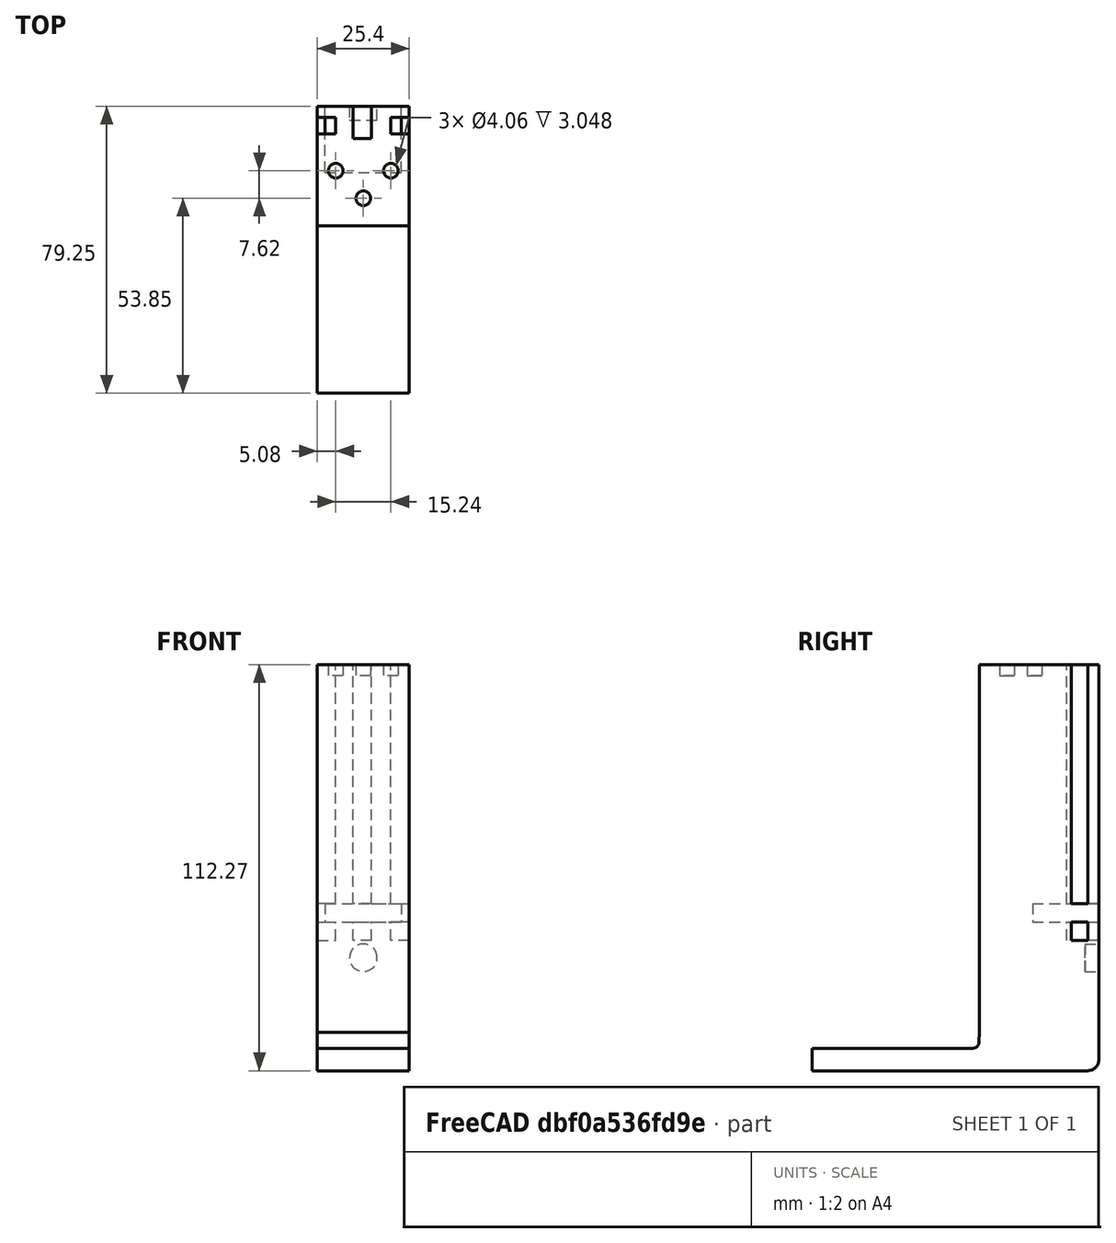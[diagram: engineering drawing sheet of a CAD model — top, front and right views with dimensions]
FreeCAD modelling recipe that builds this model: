
FCSTD DOCUMENT  (FreeCAD 0.18.1R)
Label: rail_test_crossbow_rev_02
License: All rights reserved
LicenseURL: http://en.wikipedia.org/wiki/All_rights_reserved
objects: Sketcher::SketchObject×7, PartDesign::Pad×4, PartDesign::Pocket×2, PartDesign::Hole×1, PartDesign::Body×1, Mesh::Feature×1
note: 22 computed .brp shape members not serialized (recipe doc carries the construction recipe); baked Part::Feature solids carry a one-line shape summary decoded from their .brp

FEATURE [Sketcher::SketchObject] Sketch
  MapMode = 5
  Support = -> [XY_Plane]
  sketch-geometry (17):
    g0: LineSegment StartX=0 StartY=0 StartZ=0 EndX=12.7 EndY=0 EndZ=0
    g1: LineSegment StartX=0 StartY=0 StartZ=0 EndX=-12.7 EndY=0 EndZ=0
    g2: LineSegment StartX=-12.7 StartY=0 StartZ=0 EndX=-12.7 EndY=25.4 EndZ=0
    g3: LineSegment StartX=12.7 StartY=0 StartZ=0 EndX=12.7 EndY=25.4 EndZ=0
    g4: LineSegment StartX=-12.7 StartY=25.4 StartZ=0 EndX=-7.62 EndY=25.4 EndZ=0
    g5: LineSegment StartX=-7.62 StartY=25.4 StartZ=0 EndX=-7.62 EndY=29.972 EndZ=0
    g6: LineSegment StartX=12.7 StartY=25.4 StartZ=0 EndX=7.62 EndY=25.4 EndZ=0
    g7: LineSegment StartX=7.62 StartY=25.4 StartZ=0 EndX=7.62 EndY=29.972 EndZ=0
    g8: LineSegment StartX=7.62 StartY=29.972 StartZ=0 EndX=12.7 EndY=29.972 EndZ=0
    g9: LineSegment StartX=-7.62 StartY=29.972 StartZ=0 EndX=-12.7 EndY=29.972 EndZ=0
    g10: LineSegment StartX=-12.7 StartY=29.972 StartZ=0 EndX=-12.7 EndY=33.02 EndZ=0
    g11: LineSegment StartX=12.7 StartY=29.972 StartZ=0 EndX=12.7 EndY=33.02 EndZ=0
    g12: LineSegment StartX=-12.7 StartY=33.02 StartZ=0 EndX=-2.794 EndY=33.02 EndZ=0
    g13: LineSegment StartX=-2.794 StartY=33.02 StartZ=0 EndX=-2.794 EndY=24.13 EndZ=0
    g14: LineSegment StartX=-2.794 StartY=24.13 StartZ=0 EndX=2.286 EndY=24.13 EndZ=0
    g15: LineSegment StartX=2.286 StartY=24.13 StartZ=0 EndX=2.286 EndY=33.02 EndZ=0
    g16: LineSegment StartX=12.7 StartY=33.02 StartZ=0 EndX=2.286 EndY=33.02 EndZ=0
  constraints (50):
    c: Coincident(g0,g-1)
    c: PointOnObject(g0,g-1)
    c: Coincident(g1,g0)
    c: PointOnObject(g1,g-1)
    c: Coincident(g2,g1)
    c: Vertical(g2)
    c: Coincident(g3,g0)
    c: Vertical(g3)
    c: Coincident(g4,g2)
    c: Horizontal(g4)
    c: Coincident(g5,g4)
    c: Vertical(g5)
    c: Coincident(g6,g3)
    c: Horizontal(g6)
    c: Coincident(g7,g6)
    c: Vertical(g7)
    c: Coincident(g8,g7)
    c: Horizontal(g8)
    c: Coincident(g9,g5)
    c: Horizontal(g9)
    c: Coincident(g10,g9)
    c: Vertical(g10)
    c: Coincident(g11,g8)
    c: Vertical(g11)
    c: DistanceY(g7,g7) = 4.572
    c: DistanceY(g5,g5) = 4.572
    c: DistanceY(g11,g11) = 3.048
    c: DistanceY(g10,g10) = 3.048
    c: Distance(g1,g0) = 25.4
    c: DistanceX(g0,g0) = 12.7
    c: DistanceX(g8,g8) = 5.08
    c: DistanceX(g9,g9) = 5.08
    c: DistanceY(g3,g3) = 25.4
    c: Coincident(g12,g10)
    c: Horizontal(g12)
    c: Coincident(g13,g12)
    c: Vertical(g13)
    c: Coincident(g14,g13)
    c: Horizontal(g14)
    c: Coincident(g15,g14)
    c: Vertical(g15)
    c: Coincident(g16,g11)
    c: Coincident(g16,g15)
    c: Horizontal(g16)
    c: DistanceX(g14,g14) = 5.08
    c: DistanceY(g15,g15) = 8.89
    c: DistanceY(g2,g2) = 25.4
    c: Distance(g14,g3) = 10.414
    c: Distance(g10,g11) = 25.4
    c: DistanceX(g3,g8) = 0
FEATURE [PartDesign::Pad] Pad
  Length = 76.2
  Length2 = 100.076
  Profile = -> Sketch
  Type = 0
FEATURE [Sketcher::SketchObject] Sketch001
  MapMode = 5
  Placement = pos=(-12.7,0,0) rot=(0.57735,-0.57735,-0.57735;2.0944rad)
  Support = -> [Pad]
  sketch-geometry (4):
    g0: LineSegment StartX=-14.732 StartY=5.08 StartZ=0 EndX=-33.02 EndY=5.08 EndZ=0
    g1: LineSegment StartX=-33.02 StartY=5.08 StartZ=0 EndX=-33.02 EndY=10.16 EndZ=0
    g2: LineSegment StartX=-33.02 StartY=10.16 StartZ=0 EndX=-14.732 EndY=10.16 EndZ=0
    g3: LineSegment StartX=-14.732 StartY=10.16 StartZ=0 EndX=-14.732 EndY=5.08 EndZ=0
  constraints (12):
    c: Horizontal(g0)
    c: Coincident(g1,g0)
    c: Vertical(g1)
    c: Coincident(g2,g1)
    c: Horizontal(g2)
    c: Coincident(g3,g2)
    c: Coincident(g3,g0)
    c: Vertical(g3)
    c: DistanceX(g0,g0) = 18.288
    c: Distance(g0,g-2) = 33.02
    c: DistanceY(g3,g3) = 5.08
    c: Distance(g0,g-1) = 5.08
FEATURE [PartDesign::Pocket] Pocket
  BaseFeature = -> Pad
  Length = 30.48
  Length2 = 100.076
  Profile = -> Sketch001
  Type = 0
FEATURE [Sketcher::SketchObject] Sketch002
  MapMode = 5
  Placement = pos=(0,0,76.2) rot=(0,0,1;0rad)
  Support = -> [Pocket]
  sketch-geometry (3):
    g0: Circle CenterX=0 CenterY=7.62 CenterZ=0 NormalX=0 NormalY=0 NormalZ=1 AngleXU=0 Radius=2.032
    g1: Circle CenterX=7.62 CenterY=15.24 CenterZ=0 NormalX=0 NormalY=0 NormalZ=1 AngleXU=0 Radius=2.032
    g2: Circle CenterX=-7.62 CenterY=15.24 CenterZ=0 NormalX=0 NormalY=0 NormalZ=1 AngleXU=0 Radius=2.032
  constraints (9):
    c: PointOnObject(g0,g-2)
    c: Radius(g0) = 2.032
    c: Radius(g1) = 2.032
    c: Radius(g2) = 2.032
    c: Distance(g0,g-1) = 7.62
    c: Distance(g1,g-2) = 7.62
    c: Distance(g1,g-1) = 15.24
    c: Distance(g2,g-1) = 15.24
    c: Distance(g2,g-2) = 7.62
FEATURE [PartDesign::Hole] Hole
  BaseFeature = -> Pocket
  Depth = 3.048
  DepthType = 0
  Diameter = 4.064
  DrillPoint = 0
  DrillPointAngle = 118
  HoleCutCountersinkAngle = 90
  HoleCutDepth = 0
  HoleCutDiameter = 0
  HoleCutType = 0
  ModelActualThread = false
  Profile = -> Sketch002
  Tapered = false
  TaperedAngle = 90
  ThreadAngle = 0
  ThreadClass = 0
  ThreadCutOffInner = 0
  ThreadCutOffOuter = 0
  ThreadDirection = 0
  ThreadFit = 0
  ThreadPitch = 0
  ThreadSize = 0
  ThreadType = 0
  Threaded = false
FEATURE [Sketcher::SketchObject] Sketch003
  MapMode = 5
  Placement = pos=(0,14.732,0) rot=(0,0.707107,0.707107;3.14159rad)
  Support = -> [Hole]
  sketch-geometry (8):
    g0: LineSegment StartX=-12.7 StartY=10.16 StartZ=0 EndX=-10.541 EndY=10.16 EndZ=0
    g1: LineSegment StartX=-10.541 StartY=10.16 StartZ=0 EndX=-10.541 EndY=5.08 EndZ=0
    g2: LineSegment StartX=-10.541 StartY=5.08 StartZ=0 EndX=-12.7 EndY=5.08 EndZ=0
    g3: LineSegment StartX=-12.7 StartY=5.08 StartZ=0 EndX=-12.7 EndY=10.16 EndZ=0
    g4: LineSegment StartX=12.7 StartY=10.16 StartZ=0 EndX=10.541 EndY=10.16 EndZ=0
    g5: LineSegment StartX=10.541 StartY=10.16 StartZ=0 EndX=10.541 EndY=5.08 EndZ=0
    g6: LineSegment StartX=10.541 StartY=5.08 StartZ=0 EndX=12.7 EndY=5.08 EndZ=0
    g7: LineSegment StartX=12.7 StartY=5.08 StartZ=0 EndX=12.7 EndY=10.16 EndZ=0
  constraints (24):
    c: Coincident(g0,g1)
    c: Coincident(g1,g2)
    c: Coincident(g2,g3)
    c: Coincident(g3,g0)
    c: Horizontal(g0)
    c: Horizontal(g2)
    c: Vertical(g1)
    c: Vertical(g3)
    c: Coincident(g4,g5)
    c: Coincident(g5,g6)
    c: Coincident(g6,g7)
    c: Coincident(g7,g4)
    c: Horizontal(g4)
    c: Horizontal(g6)
    c: Vertical(g5)
    c: Vertical(g7)
    c: Distance(g7) = 5.08
    c: Distance(g4) = 2.159
    c: Distance(g0) = 2.159
    c: Distance(g3) = 5.08
    c: Distance(g0,g-2) = 10.541
    c: Distance(g4,g-2) = 10.541
    c: Distance(g6,g-1) = 5.08
    c: Distance(g2,g-1) = 5.08
FEATURE [PartDesign::Pad] Pad001
  BaseFeature = -> Hole
  Length = 18.288
  Length2 = 100.076
  Profile = -> Sketch003
  Type = 0
FEATURE [Sketcher::SketchObject] Sketch004
  MapMode = 5
  Placement = pos=(0,0,0) rot=(1,0,0;3.14159rad)
  Support = -> [Pad001]
  sketch-geometry (4):
    g0: LineSegment StartX=-12.7 StartY=0 StartZ=0 EndX=12.7 EndY=0 EndZ=0
    g1: LineSegment StartX=12.7 StartY=0 StartZ=0 EndX=12.7 EndY=-33.02 EndZ=0
    g2: LineSegment StartX=12.7 StartY=-33.02 StartZ=0 EndX=-12.7 EndY=-33.02 EndZ=0
    g3: LineSegment StartX=-12.7 StartY=-33.02 StartZ=0 EndX=-12.7 EndY=0 EndZ=0
  constraints (12):
    c: Coincident(g0,g1)
    c: Coincident(g1,g2)
    c: Coincident(g2,g3)
    c: Coincident(g3,g0)
    c: Horizontal(g0)
    c: Horizontal(g2)
    c: Vertical(g1)
    c: Vertical(g3)
    c: PointOnObject(g0,g-1)
    c: Distance(g1) = 33.02
    c: Distance(g2) = 25.4
    c: Distance(g-1,g0) = 12.7
FEATURE [PartDesign::Pad] Pad002
  BaseFeature = -> Pad001
  Length = 25.4
  Length2 = 100.076
  Profile = -> Sketch004
  Type = 0
FEATURE [Sketcher::SketchObject] Sketch005
  MapMode = 5
  Placement = pos=(12.7,0,0) rot=(0.57735,0.57735,0.57735;2.0944rad)
  Support = -> [Pad002]
  sketch-geometry (8):
    g0: LineSegment StartX=0 StartY=-25.4 StartZ=0 EndX=-0.0301127 EndY=-27.94 EndZ=0
    g1: LineSegment StartX=0 StartY=-25.4 StartZ=0 EndX=33.02 EndY=-25.4 EndZ=0
    g2: LineSegment StartX=33.02 StartY=-25.4 StartZ=0 EndX=33.02 EndY=-33.02 EndZ=0
    g3: LineSegment StartX=-2.032 StartY=-29.9183 StartZ=0 EndX=-46.228 EndY=-29.9183 EndZ=0
    g4: LineSegment StartX=29.972 StartY=-36.068 StartZ=0 EndX=-46.228 EndY=-36.068 EndZ=0
    g5: LineSegment StartX=-46.228 StartY=-36.068 StartZ=0 EndX=-46.228 EndY=-29.9183 EndZ=0
    g6: ArcOfCircle CenterX=-2.032 CenterY=-27.9163 CenterZ=0 NormalX=0 NormalY=0 NormalZ=1 AngleXU=0 Radius=2.00203 StartAngle=4.71239 EndAngle=6.27133
    g7: ArcOfCircle CenterX=29.972 CenterY=-33.02 CenterZ=0 NormalX=0 NormalY=0 NormalZ=1 AngleXU=0 Radius=3.048 StartAngle=4.71239 EndAngle=6.28319
  constraints (22):
    c: PointOnObject(g0,g-2)
    c: Coincident(g1,g0)
    c: Horizontal(g1)
    c: Coincident(g2,g1)
    c: Vertical(g2)
    c: Horizontal(g3)
    c: Horizontal(g4)
    c: Coincident(g5,g4)
    c: Coincident(g5,g3)
    c: Vertical(g5)
    c: Distance(g1) = 33.02
    c: Distance(g0,g-1) = 25.4
    c: Tangent(g0,g6) = 1.5708
    c: Tangent(g3,g6) = 1.5708
    c: Tangent(g2,g7) = 1.5708
    c: Tangent(g4,g7) = 1.5708
    c: DistanceX(g4,g4) = 76.2
    c: DistanceX(g3,g3) = 44.196
    c: DistanceY(g0,g0) = 2.54
    c: DistanceY(g2,g2) = 7.62
    c: Radius(g6) = 2.00203
    c: Radius(g7) = 3.048
FEATURE [PartDesign::Pad] Pad003
  BaseFeature = -> Pad002
  Length = 25.4
  Length2 = 100.076
  Profile = -> Sketch005
  Reversed = true
  Type = 0
FEATURE [Sketcher::SketchObject] Sketch006
  MapMode = 5
  Placement = pos=(0,33.02,0) rot=(0,0.707107,0.707107;3.14159rad)
  Support = -> [Pad003]
  sketch-geometry (1):
    g0: Circle CenterX=0 CenterY=-4.826 CenterZ=0 NormalX=0 NormalY=0 NormalZ=1 AngleXU=0 Radius=3.81
  constraints (3):
    c: PointOnObject(g0,g-2)
    c: Radius(g0) = 3.81
    c: Distance(g-1,g0) = 4.826
FEATURE [PartDesign::Pocket] Pocket001
  BaseFeature = -> Pad003
  Length = 3.81
  Length2 = 100.076
  Profile = -> Sketch006
  Type = 0
FEATURE [PartDesign::Body] Body
  Group = -> [Sketch,Pad,Sketch001,Pocket,Sketch002,Hole,Sketch003,Pad001,Sketch004,Pad002,Sketch005,Pad003,Sketch006,Pocket001]
  Origin = -> Origin
  Tip = -> Pocket001
FEATURE [Mesh::Feature] Mesh  label="Pocket001 (Meshed)"
